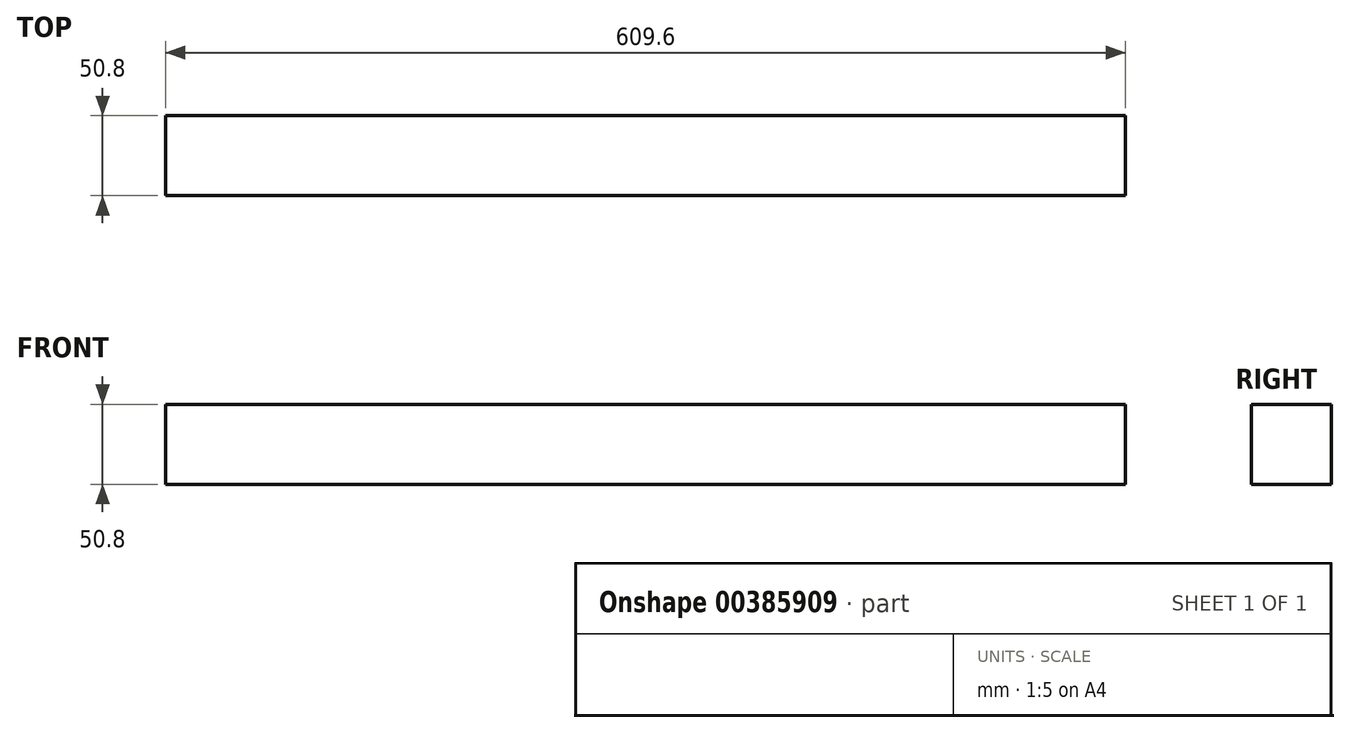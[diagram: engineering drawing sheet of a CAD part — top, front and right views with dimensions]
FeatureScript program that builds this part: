
annotation { "Feature Type Name" : "Feature", "Feature Type Description" : "" }
export const myFeature = defineFeature(function(context is Context, id is Id, definition is map)
    precondition{}
    {
        {
            var Q0;
            Q0=qCreatedBy(makeId("Front.planeOp"),FACE);
            var sketch = newSketch(context, id + "F0", { "sketchPlane" : qUnion([Q0])});
            skLineSegment(sketch, "E0.bottom", {"start": v(0, 0) * mm, "end": v(609.6, 0) * mm});
            skLineSegment(sketch, "E0.top", {"start": v(0, 50.8) * mm, "end": v(609.6, 50.8) * mm});
            skLineSegment(sketch, "E0.left", {"start": v(0, 0) * mm, "end": v(0, 50.8) * mm});
            skLineSegment(sketch, "E0.right", {"start": v(609.6, 0) * mm, "end": v(609.6, 50.8) * mm});
            skPoint(sketch, "E1.1.internal.snap0", {"position": v(0, 25.4) * mm});
            skFitSpline(sketch, "E1", {"points": [v(0, 25.4) * mm, v(48.66, 25.4) * mm, v(559.78, 254) * mm], "startDerivative": vector(147.24, -24.16) * mm, "endDerivative": vector(504.17, 228.7) * mm});
            skSolve(sketch);
        }
        {
            var Q0;
            Q0 = qSketchRegion(id + "F0", true);
            extrude(context, id + "F1", {"entities" : qUnion([Q0]), "depth" : 50.8 * mm});
        }
    });
